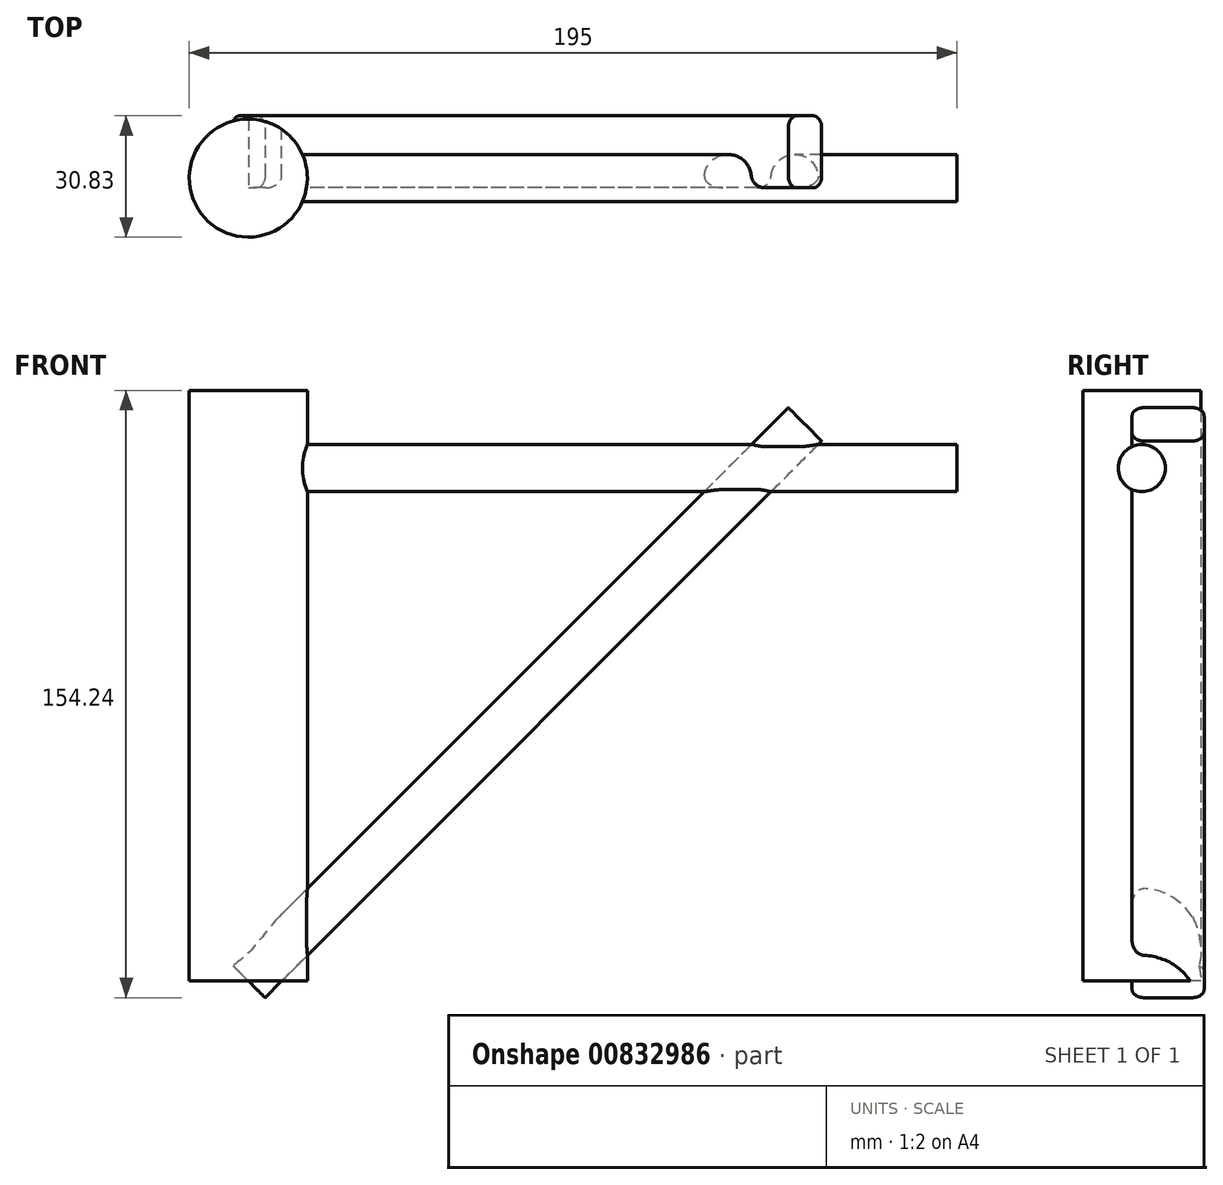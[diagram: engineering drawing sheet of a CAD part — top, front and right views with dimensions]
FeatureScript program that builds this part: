
annotation { "Feature Type Name" : "Feature", "Feature Type Description" : "" }
export const myFeature = defineFeature(function(context is Context, id is Id, definition is map)
    precondition{}
    {
        {
            var Q0;
            Q0=qCreatedBy(makeId("Top.planeOp"),FACE);
            var sketch = newSketch(context, id + "F0", { "sketchPlane" : qUnion([Q0])});
            skCircle(sketch, "E0", {"center": v(0, 0) * mm, "radius": 15 * mm});
            skSolve(sketch);
        }
        {
            var Q0;
            Q0=makeQuery(id+"F0.imprint","IMPRINT",FACE,{"disambiguationData":[TD([[makeQuery(id+"F0.imprint","IMPRINT",EDGE,{"derivedFrom":sQuery(id+"F0.wireOp",EDGE,"E0")}),1.0]])]});
            extrude(context, id + "F1", {"entities" : qUnion([Q0]), "depth" : 150 * mm, "offsetDistance" : 25 * mm});
        }
        {
            var Q0;
            Q0=qCreatedBy(makeId("Right.planeOp"),FACE);
            var sketch = newSketch(context, id + "F2", { "sketchPlane" : qUnion([Q0])});
            skCircle(sketch, "E1", {"center": v(0, 130.32) * mm, "radius": 6 * mm});
            skSolve(sketch);
        }
        {
            var Q0;
            Q0 = qSketchRegion(id + "F2", true);
            extrude(context, id + "F3", {"entities" : qUnion([Q0]), "operationType" : NewBodyOperationType.ADD, "depth" : 180 * mm, "offsetDistance" : 25 * mm});
        }
        {
            var Q0;
            Q0=qCreatedBy(makeId("Top.planeOp"),FACE);
            var sketch = newSketch(context, id + "F4", { "sketchPlane" : qUnion([Q0])});
            skLineSegment(sketch, "E2", {"start": v(0, 45.59) * mm, "end": v(0, -41.23) * mm});
            skSolve(sketch);
        }
        {
            var Q0;
            Q0=qCreatedBy(makeId("Top.planeOp"),FACE);
            var Q1;
            Q1=sQuery(id+"F4.wireOp",EDGE,"E2");
            cPlane(context, id + "F5", {"entities" : qUnion([Q0, Q1]), "cplaneType" : CPlaneType.LINE_ANGLE, "offset" : 50 * mm, "angle" : 45 * degree, "oppositeDirection" : true, "width" : 150 * mm, "height" : 150 * mm});
        }
        {
            var Q0;
            Q0=qCreatedBy(id+"F5.planeOp",FACE);
            var sketch = newSketch(context, id + "F6", { "sketchPlane" : qUnion([Q0])});
            skLineSegment(sketch, "E3.bottom", {"start": v(-12.83, 6) * mm, "end": v(-0.52, 6) * mm});
            skLineSegment(sketch, "E3.top", {"start": v(-12.83, -6) * mm, "end": v(-0.52, -6) * mm});
            skLineSegment(sketch, "E3.left", {"start": v(-15.83, 3) * mm, "end": v(-15.83, -3) * mm});
            skLineSegment(sketch, "E3.right", {"start": v(2.48, 3) * mm, "end": v(2.48, -3) * mm});
            skPoint(sketch, "E4.visualSharp", {"position": v(-15.83, 6) * mm});
            skArc(sketch, "E4.filletArc", {"start": v(-12.83, 6) * mm, "mid": v(-14.95, 5.12) * mm, "end": v(-15.83, 3) * mm});
            skPoint(sketch, "E5.visualSharp", {"position": v(-15.83, -6) * mm});
            skArc(sketch, "E5.filletArc", {"start": v(-15.83, -3) * mm, "mid": v(-14.95, -5.12) * mm, "end": v(-12.83, -6) * mm});
            skPoint(sketch, "E6.visualSharp", {"position": v(2.48, 6) * mm});
            skArc(sketch, "E6.filletArc", {"start": v(2.48, 3) * mm, "mid": v(1.6, 5.12) * mm, "end": v(-0.52, 6) * mm});
            skPoint(sketch, "E7.visualSharp", {"position": v(2.48, -6) * mm});
            skArc(sketch, "E7.filletArc", {"start": v(-0.52, -6) * mm, "mid": v(1.6, -5.12) * mm, "end": v(2.48, -3) * mm});
            skSolve(sketch);
        }
        {
            var Q0;
            Q0 = qSketchRegion(id + "F6", true);
            extrude(context, id + "F7", {"entities" : qUnion([Q0]), "operationType" : NewBodyOperationType.ADD, "oppositeDirection" : true, "depth" : 200 * mm, "offsetDistance" : 25 * mm});
        }
    });
